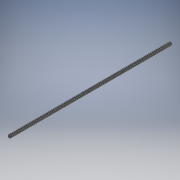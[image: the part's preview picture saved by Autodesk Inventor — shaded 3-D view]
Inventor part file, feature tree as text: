
AUTODESK INVENTOR PART (.ipt)
format: ipt  version: 2018 (Build 220112000, 112)  size: 194,560 bytes
history: native  units: in
note: dims shown in document units (in); Inventor stores cm internally (conversion verified against a paired STEP export)
features: fillet x1
ambient origin geometry x8: Origin, YZ Plane, XZ Plane, XY Plane, X Axis, Y Axis, Z Axis, Center Point
bodies: Solid1 (feature_tree)
feature tree (1):
  fillet  "Fillet6"  [1 undecoded]
note: 1 required parameter value undecoded (feature->parameter linkage not recoverable at this tier; creation-order binding heuristic only, values carry confidence <= 0.55)
